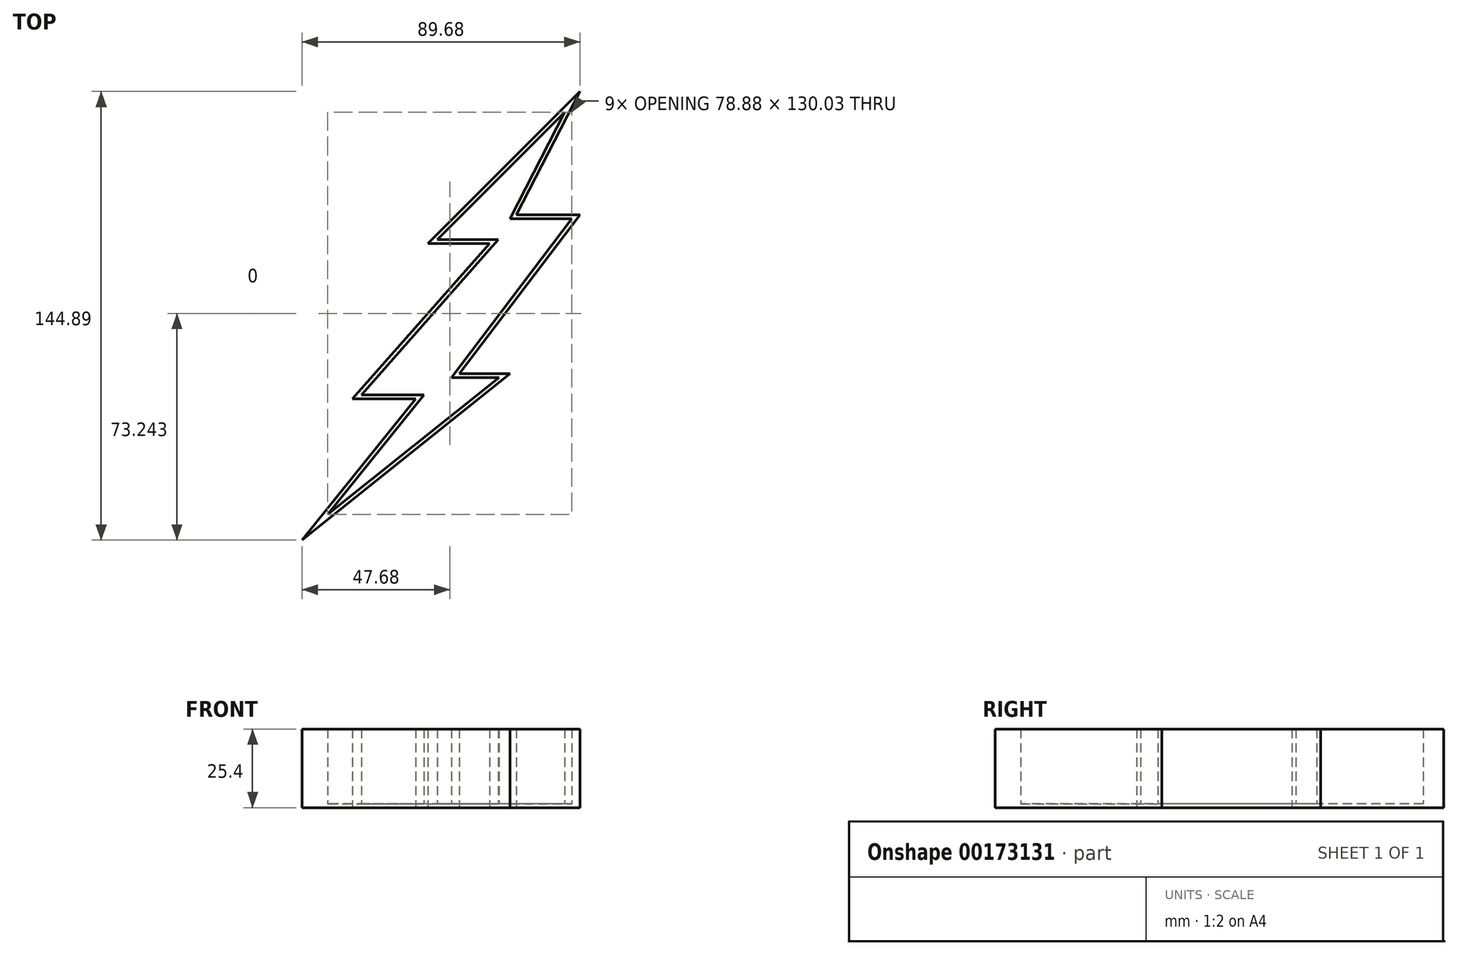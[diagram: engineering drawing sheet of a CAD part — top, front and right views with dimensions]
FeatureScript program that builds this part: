
annotation { "Feature Type Name" : "Feature", "Feature Type Description" : "" }
export const myFeature = defineFeature(function(context is Context, id is Id, definition is map)
    precondition{}
    {
        {
            var Q0;
            Q0=qCreatedBy(makeId("Top.planeOp"),FACE);
            var sketch = newSketch(context, id + "F0", { "sketchPlane" : qUnion([Q0])});
            skLineSegment(sketch, "E0", {"start": v(32.23, 68.8) * mm, "end": v(-16.81, 19.76) * mm});
            skLineSegment(sketch, "E1", {"start": v(-16.81, 19.76) * mm, "end": v(3.08, 19.76) * mm});
            skLineSegment(sketch, "E2", {"start": v(3.08, 19.76) * mm, "end": v(-41.2, -30.4) * mm});
            skLineSegment(sketch, "E3", {"start": v(-41.2, -30.4) * mm, "end": v(-20.74, -30.4) * mm});
            skLineSegment(sketch, "E4", {"start": v(-20.74, -30.4) * mm, "end": v(-57.45, -76.09) * mm});
            skLineSegment(sketch, "E5", {"start": v(32.23, 68.8) * mm, "end": v(11.77, 29) * mm});
            skLineSegment(sketch, "E6", {"start": v(11.77, 29) * mm, "end": v(32.23, 29) * mm});
            skLineSegment(sketch, "E7", {"start": v(32.23, 29) * mm, "end": v(-6.73, -22.28) * mm});
            skLineSegment(sketch, "E8", {"start": v(-6.73, -22.28) * mm, "end": v(9.74, -22.28) * mm});
            skLineSegment(sketch, "E9", {"start": v(-57.45, -76.09) * mm, "end": v(9.74, -22.28) * mm});
            skSolve(sketch);
        }
        {
            var Q0;
            Q0=makeQuery(id+"F0.imprint","IMPRINT",FACE,{"disambiguationData":[TD([[makeQuery(id+"F0.imprint","IMPRINT",EDGE,{"derivedFrom":sQuery(id+"F0.wireOp",EDGE,"E0")}),1.0]])]});
            extrude(context, id + "F1", {"entities" : qUnion([Q0]), "depth" : 25.4 * mm});
        }
        {
            var Q0;
            Q0=makeQuery(id+"F1.opExtrude","CAP_FACE",FACE,{"disambiguationData":[OSD([sQuery(id+"F0.wireOp",EDGE,"E0"),sQuery(id+"F0.wireOp",EDGE,"E1"),sQuery(id+"F0.wireOp",EDGE,"E2"),sQuery(id+"F0.wireOp",EDGE,"E3"),sQuery(id+"F0.wireOp",EDGE,"E4"),sQuery(id+"F0.wireOp",EDGE,"E5"),sQuery(id+"F0.wireOp",EDGE,"E6"),sQuery(id+"F0.wireOp",EDGE,"E7"),sQuery(id+"F0.wireOp",EDGE,"E8"),sQuery(id+"F0.wireOp",EDGE,"E9")])],"isStart":false});
            shell(context, id + "F2", {"entities" : qUnion([Q0]), "thickness" : 1.27 * mm});
        }
    });
